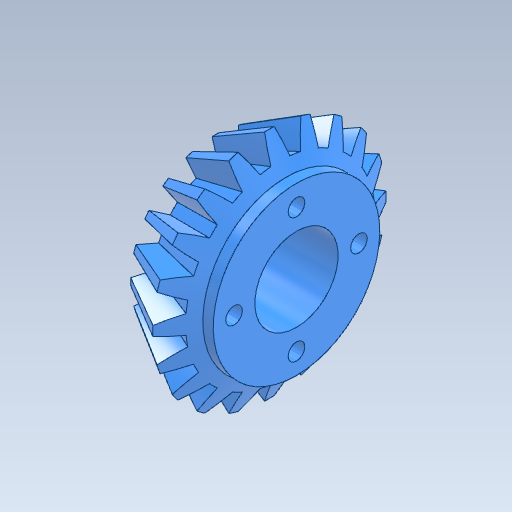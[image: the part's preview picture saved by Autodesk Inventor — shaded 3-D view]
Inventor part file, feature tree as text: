
AUTODESK INVENTOR PART (.ipt)
format: ipt  version: 2024 (Build 280153000, 153)  size: 508,928 bytes
history: native  units: mm
features: other x3, sketch x2, revolve x1, extrude x1
ambient origin geometry x8: Origin, YZ Plane, XZ Plane, XY Plane, X Axis, Y Axis, Z Axis, Center Point
bodies: Solid1_1 (feature_tree)
feature tree (7):
  other  "_PB1-2040_On.ipt"
  sketch  "スケッチ1"
  sketch  "スケッチ2"
  revolve  "回転1"
  extrude  "押し出し1"  Depth=40.0mm TaperAngle=360.0deg
  other  "Solid1::_PB1-2040_On.ipt"
  other  "TaggingFeature2"
